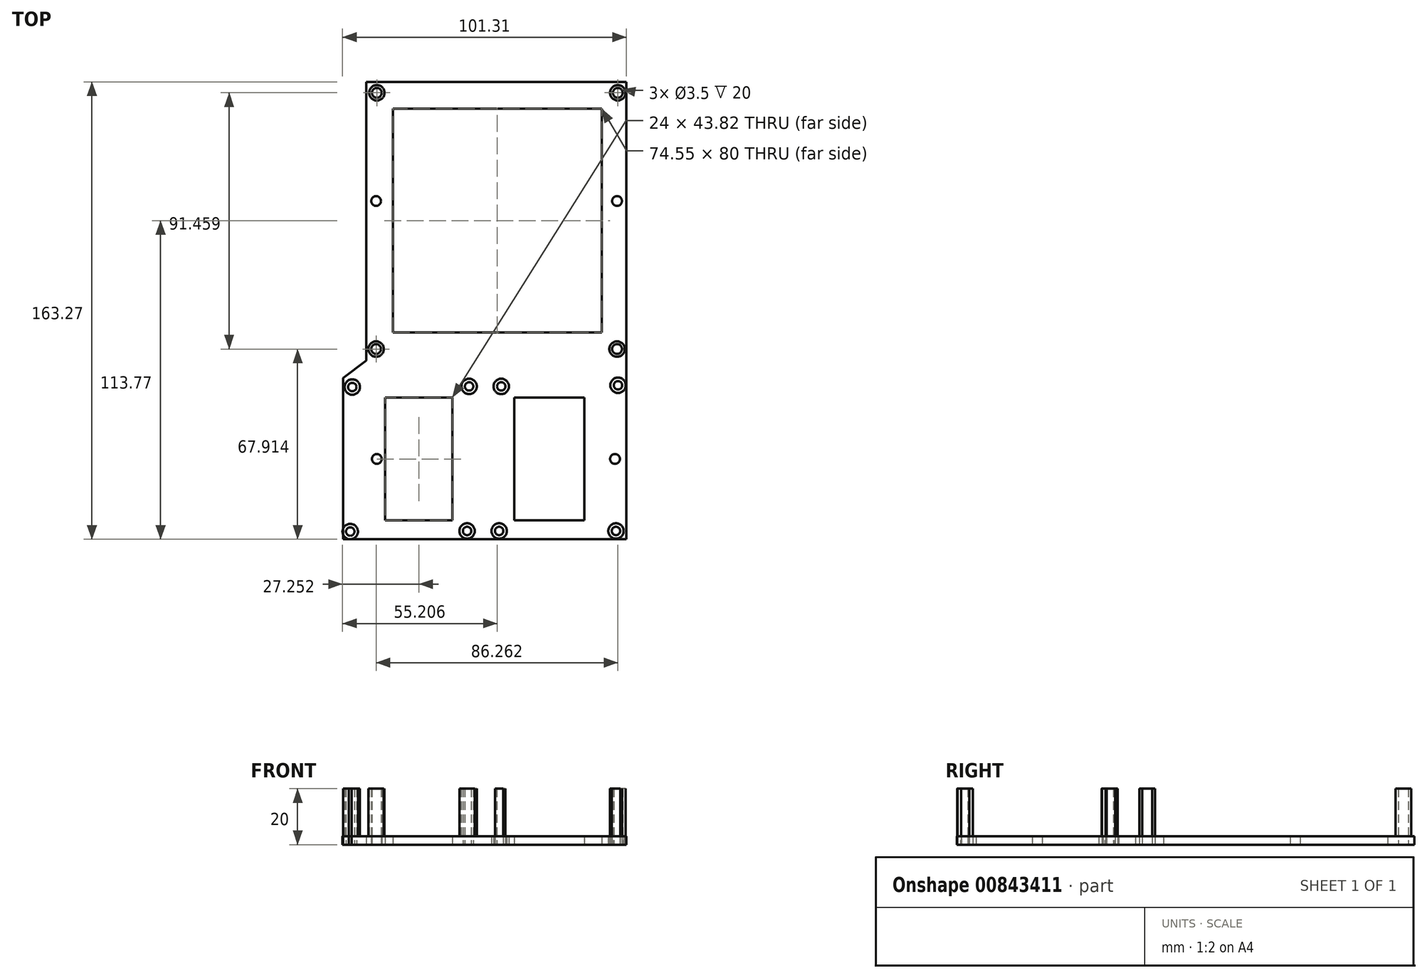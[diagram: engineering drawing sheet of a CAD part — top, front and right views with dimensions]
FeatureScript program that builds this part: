
annotation { "Feature Type Name" : "Feature", "Feature Type Description" : "" }
export const myFeature = defineFeature(function(context is Context, id is Id, definition is map)
    precondition{}
    {
        {
            var Q0;
            Q0=qCreatedBy(makeId("Top.planeOp"),FACE);
            var sketch = newSketch(context, id + "F0", { "sketchPlane" : qUnion([Q0])});
            skLineSegment(sketch, "E0.bottom", {"start": v(-33.05, 72.5) * mm, "end": v(41.5, 72.5) * mm});
            skLineSegment(sketch, "E0.top", {"start": v(-33.05, -7.5) * mm, "end": v(41.5, -7.5) * mm});
            skLineSegment(sketch, "E0.left", {"start": v(-33.05, 72.5) * mm, "end": v(-33.05, -7.5) * mm});
            skLineSegment(sketch, "E0.right", {"start": v(41.5, 72.5) * mm, "end": v(41.5, -7.5) * mm});
            skLineSegment(sketch, "E1.bottom", {"start": v(-35.73, -30.68) * mm, "end": v(-11.73, -30.68) * mm});
            skLineSegment(sketch, "E1.top", {"start": v(-35.73, -74.5) * mm, "end": v(-11.73, -74.5) * mm});
            skLineSegment(sketch, "E1.left", {"start": v(-35.73, -30.68) * mm, "end": v(-35.73, -74.5) * mm});
            skLineSegment(sketch, "E1.right", {"start": v(-11.73, -30.68) * mm, "end": v(-11.73, -74.5) * mm});
            skCircle(sketch, "E2", {"center": v(-38.74, 78.1) * mm, "radius": 1.75 * mm});
            skCircle(sketch, "E3", {"center": v(47.26, 78.1) * mm, "radius": 1.75 * mm});
            skCircle(sketch, "E4", {"center": v(-39, -13.36) * mm, "radius": 1.75 * mm});
            skCircle(sketch, "E5", {"center": v(-48.23, -78.52) * mm, "radius": 1.5 * mm});
            skCircle(sketch, "E6", {"center": v(-47.5, -26.92) * mm, "radius": 1.5 * mm});
            skCircle(sketch, "E7", {"center": v(-5.8, -26.7) * mm, "radius": 1.5 * mm});
            skCircle(sketch, "E8", {"center": v(-6.53, -78.3) * mm, "radius": 1.5 * mm});
            skCircle(sketch, "E9.MirrorC", {"center": v(5.65, -26.7) * mm, "radius": 1.5 * mm});
            skCircle(sketch, "E10.MirrorC", {"center": v(47.35, -26.3) * mm, "radius": 1.5 * mm});
            skCircle(sketch, "E11.MirrorC", {"center": v(46.62, -78.3) * mm, "radius": 1.5 * mm});
            skCircle(sketch, "E12.MirrorC", {"center": v(4.92, -78.3) * mm, "radius": 1.5 * mm});
            skLineSegment(sketch, "E13.MirrorCS", {"start": v(35.27, -74.5) * mm, "end": v(10.27, -74.5) * mm});
            skLineSegment(sketch, "E14.MirrorCS", {"start": v(35.27, -30.68) * mm, "end": v(35.27, -74.5) * mm});
            skLineSegment(sketch, "E15.MirrorCS", {"start": v(35.27, -30.68) * mm, "end": v(10.27, -30.68) * mm});
            skCircle(sketch, "E16", {"center": v(-38.74, 78.1) * mm, "radius": 2.75 * mm});
            skCircle(sketch, "E17", {"center": v(47.26, 78.1) * mm, "radius": 2.75 * mm});
            skCircle(sketch, "E18", {"center": v(47.35, -26.3) * mm, "radius": 2.75 * mm});
            skCircle(sketch, "E19", {"center": v(5.65, -26.7) * mm, "radius": 2.75 * mm});
            skCircle(sketch, "E20", {"center": v(-5.8, -26.7) * mm, "radius": 2.75 * mm});
            skCircle(sketch, "E21", {"center": v(-47.5, -26.92) * mm, "radius": 2.75 * mm});
            skCircle(sketch, "E22", {"center": v(-48.23, -78.52) * mm, "radius": 2.75 * mm});
            skCircle(sketch, "E23", {"center": v(-6.53, -78.3) * mm, "radius": 2.75 * mm});
            skCircle(sketch, "E24", {"center": v(4.92, -78.3) * mm, "radius": 2.75 * mm});
            skCircle(sketch, "E25", {"center": v(46.62, -78.3) * mm, "radius": 2.75 * mm});
            skCircle(sketch, "E26", {"center": v(-39, 39.47) * mm, "radius": 1.75 * mm});
            skCircle(sketch, "E27", {"center": v(47, 39.47) * mm, "radius": 1.75 * mm});
            skCircle(sketch, "E28", {"center": v(-38.74, -52.6) * mm, "radius": 1.75 * mm});
            skCircle(sketch, "E29", {"center": v(46.27, -52.6) * mm, "radius": 1.75 * mm});
            skPoint(sketch, "E30", {"position": v(0, 0) * mm});
            skLineSegment(sketch, "E31", {"start": v(10.27, -74.5) * mm, "end": v(10.27, -30.68) * mm});
            skCircle(sketch, "E32.MirrorC", {"center": v(47, -13.36) * mm, "radius": 1.75 * mm});
            skCircle(sketch, "E33.MirrorC", {"center": v(47, -13.36) * mm, "radius": 2.75 * mm});
            skLineSegment(sketch, "E34.top", {"start": v(-50.73, -81.21) * mm, "end": v(50.27, -81.21) * mm});
            skLineSegment(sketch, "E34.left", {"start": v(-50.73, -23.67) * mm, "end": v(-50.73, -81.21) * mm});
            skCircle(sketch, "E35", {"center": v(-39, -13.36) * mm, "radius": 2.75 * mm});
            skLineSegment(sketch, "E36.bottom", {"start": v(-42.55, 82) * mm, "end": v(50.33, 82) * mm});
            skLineSegment(sketch, "E36.left", {"start": v(-42.55, 82) * mm, "end": v(-42.55, -17.5) * mm});
            skLineSegment(sketch, "E37", {"start": v(-42.55, -17.5) * mm, "end": v(-50.73, -23.67) * mm});
            skLineSegment(sketch, "E38", {"start": v(-38.74, 78.1) * mm, "end": v(-38.74, -88.5) * mm, "construction": true});
            skLineSegment(sketch, "E39", {"start": v(50.33, 82) * mm, "end": v(50.27, -81.21) * mm});
            skSolve(sketch);
        }
        {
            var Q0;
            Q0 = qSketchRegion(id + "F0", true);
            extrude(context, id + "F1", {"entities" : qUnion([Q0]), "depth" : 3 * mm, "offsetDistance" : 25 * mm});
        }
        {
            var Q0;
            Q0=makeQuery(id+"F0.imprint","IMPRINT",FACE,{"disambiguationData":[TD([[makeQuery(id+"F0.imprint","IMPRINT",EDGE,{"derivedFrom":sQuery(id+"F0.wireOp",EDGE,"E2")}),-1.0]])]});
            extrude(context, id + "F2", {"entities" : qUnion([Q0]), "operationType" : NewBodyOperationType.ADD, "depth" : 20 * mm, "offsetDistance" : 25 * mm});
        }
        {
            var Q0;
            Q0=makeQuery(id+"F0.imprint","IMPRINT",FACE,{"disambiguationData":[TD([[makeQuery(id+"F0.imprint","IMPRINT",EDGE,{"derivedFrom":sQuery(id+"F0.wireOp",EDGE,"E3")}),-1.0]])]});
            var Q1;
            Q1=makeQuery(id+"F0.imprint","IMPRINT",FACE,{"disambiguationData":[TD([[makeQuery(id+"F0.imprint","IMPRINT",EDGE,{"derivedFrom":sQuery(id+"F0.wireOp",EDGE,"E4")}),-1.0]])]});
            var Q2;
            Q2=makeQuery(id+"F0.imprint","IMPRINT",FACE,{"disambiguationData":[TD([[makeQuery(id+"F0.imprint","IMPRINT",EDGE,{"derivedFrom":sQuery(id+"F0.wireOp",EDGE,"hgA1HAhj-qqGk-2pEN-fFJD-7K3AzLAzVtDP")}),-1.0]])]});
            var Q3;
            Q3=makeQuery(id+"F0.imprint","IMPRINT",FACE,{"disambiguationData":[TD([[makeQuery(id+"F0.imprint","IMPRINT",EDGE,{"derivedFrom":sQuery(id+"F0.wireOp",EDGE,"E10.MirrorC")}),1.0]])]});
            var Q4;
            Q4=makeQuery(id+"F0.imprint","IMPRINT",FACE,{"disambiguationData":[TD([[makeQuery(id+"F0.imprint","IMPRINT",EDGE,{"derivedFrom":sQuery(id+"F0.wireOp",EDGE,"E9.MirrorC")}),1.0]])]});
            var Q5;
            Q5=makeQuery(id+"F0.imprint","IMPRINT",FACE,{"disambiguationData":[TD([[makeQuery(id+"F0.imprint","IMPRINT",EDGE,{"derivedFrom":sQuery(id+"F0.wireOp",EDGE,"E7")}),-1.0]])]});
            var Q6;
            Q6=makeQuery(id+"F0.imprint","IMPRINT",FACE,{"disambiguationData":[TD([[makeQuery(id+"F0.imprint","IMPRINT",EDGE,{"derivedFrom":sQuery(id+"F0.wireOp",EDGE,"E6")}),-1.0]])]});
            var Q7;
            Q7=makeQuery(id+"F0.imprint","IMPRINT",FACE,{"disambiguationData":[TD([[makeQuery(id+"F0.imprint","IMPRINT",EDGE,{"derivedFrom":sQuery(id+"F0.wireOp",EDGE,"E5")}),-1.0]])]});
            var Q8;
            Q8=makeQuery(id+"F0.imprint","IMPRINT",FACE,{"disambiguationData":[TD([[makeQuery(id+"F0.imprint","IMPRINT",EDGE,{"derivedFrom":sQuery(id+"F0.wireOp",EDGE,"E8")}),-1.0]])]});
            var Q9;
            Q9=makeQuery(id+"F0.imprint","IMPRINT",FACE,{"disambiguationData":[TD([[makeQuery(id+"F0.imprint","IMPRINT",EDGE,{"derivedFrom":sQuery(id+"F0.wireOp",EDGE,"E12.MirrorC")}),1.0]])]});
            var Q10;
            Q10=makeQuery(id+"F0.imprint","IMPRINT",FACE,{"disambiguationData":[TD([[makeQuery(id+"F0.imprint","IMPRINT",EDGE,{"derivedFrom":sQuery(id+"F0.wireOp",EDGE,"E11.MirrorC")}),1.0]])]});
            var Q11;
            Q11=makeQuery(id+"F0.imprint","IMPRINT",FACE,{"disambiguationData":[TD([[makeQuery(id+"F0.imprint","IMPRINT",EDGE,{"derivedFrom":sQuery(id+"F0.wireOp",EDGE,"E32.MirrorC")}),1.0]])]});
            extrude(context, id + "F3", {"entities" : qUnion([Q0, Q1, Q2, Q3, Q4, Q5, Q6, Q7, Q8, Q9, Q10, Q11]), "operationType" : NewBodyOperationType.ADD, "depth" : 20 * mm, "offsetDistance" : 25 * mm});
        }
    });
